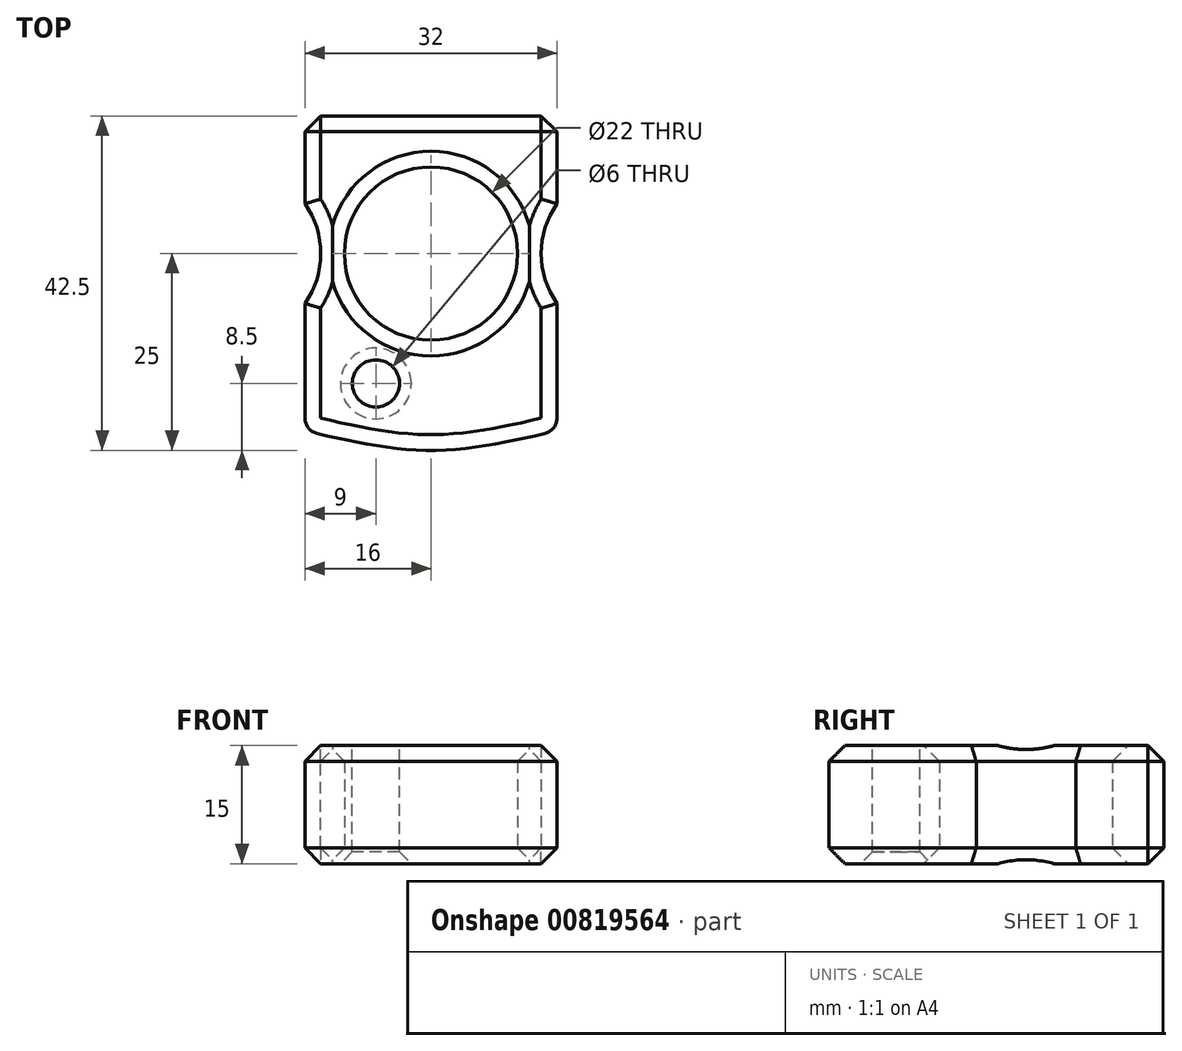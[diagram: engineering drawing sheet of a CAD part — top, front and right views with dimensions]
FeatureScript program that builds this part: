
annotation { "Feature Type Name" : "Feature", "Feature Type Description" : "" }
export const myFeature = defineFeature(function(context is Context, id is Id, definition is map)
    precondition{}
    {
        {
            var Q0;
            Q0=qCreatedBy(makeId("Top.planeOp"),FACE);
            var sketch = newSketch(context, id + "F0", { "sketchPlane" : qUnion([Q0])});
            skCircle(sketch, "E0", {"center": v(0, 0) * mm, "radius": 11 * mm});
            skLineSegment(sketch, "E1.left", {"start": v(16, -22.5) * mm, "end": v(16, -6.32) * mm});
            skLineSegment(sketch, "E1.right", {"start": v(-16, -22.5) * mm, "end": v(-16, -6.32) * mm});
            skArc(sketch, "E2", {"start": v(16, 6.32) * mm, "mid": v(14, 0) * mm, "end": v(16, -6.32) * mm});
            skArc(sketch, "E3", {"start": v(-16, -6.32) * mm, "mid": v(-14, 0) * mm, "end": v(-16, 6.32) * mm});
            skLineSegment(sketch, "E4.trimOffspring", {"start": v(-16, 6.32) * mm, "end": v(-16, 17.5) * mm});
            skLineSegment(sketch, "E5.trimOffspring", {"start": v(16, 6.32) * mm, "end": v(16, 17.5) * mm});
            skLineSegment(sketch, "E6", {"start": v(-11.23, -25) * mm, "end": v(12.92, -25) * mm, "construction": true});
            skLineSegment(sketch, "E7", {"start": v(-16, 17.5) * mm, "end": v(16, 17.5) * mm});
            skPoint(sketch, "E1.top.end.orphan", {"position": v(-16, 22.5) * mm});
            skPoint(sketch, "E1.top.start.orphan", {"position": v(16, 22.5) * mm});
            skFitSpline(sketch, "E8", {"points": [v(16, -22.5) * mm, v(0, -25) * mm, v(-16, -22.5) * mm], "startDerivative": vector(-32, -7.5) * mm, "endDerivative": vector(-32, 7.5) * mm});
            skSolve(sketch);
        }
        {
            var Q0;
            Q0 = qSketchRegion(id + "F0", true);
            extrude(context, id + "F1", {"entities" : qUnion([Q0]), "depth" : 15 * mm, "offsetDistance" : 25 * mm});
        }
        {
            var Q0;
            Q0=makeQuery(id+"F1.opExtrude","SWEPT_EDGE",EDGE,{"disambiguationData":[OSD([sQuery(id+"F0.wireOp",EDGE,"E1.right"),sQuery(id+"F0.wireOp",EDGE,"E8")])]});
            var Q1;
            Q1=makeQuery(id+"F1.opExtrude","SWEPT_EDGE",EDGE,{"disambiguationData":[OSD([sQuery(id+"F0.wireOp",EDGE,"E1.left"),sQuery(id+"F0.wireOp",EDGE,"E8")])]});
            fillet(context, id + "F2", {"entities" : qUnion([Q0, Q1]), "radius" : 2 * mm, "tangentPropagation" : true, "allowEdgeOverflow" : false});
        }
        {
            var Q0;
            Q0=makeQuery(id+"F1.opExtrude","CAP_FACE",FACE,{"disambiguationData":[OSD([sQuery(id+"F0.wireOp",EDGE,"E0"),sQuery(id+"F0.wireOp",EDGE,"E1.left"),sQuery(id+"F0.wireOp",EDGE,"E1.right"),sQuery(id+"F0.wireOp",EDGE,"E2"),sQuery(id+"F0.wireOp",EDGE,"E3"),sQuery(id+"F0.wireOp",EDGE,"E4.trimOffspring"),sQuery(id+"F0.wireOp",EDGE,"E5.trimOffspring"),sQuery(id+"F0.wireOp",EDGE,"E7"),sQuery(id+"F0.wireOp",EDGE,"E8")])],"isStart":false});
            var Q1;
            Q1=makeQuery(id+"F1.opExtrude","CAP_FACE",FACE,{"disambiguationData":[OSD([sQuery(id+"F0.wireOp",EDGE,"E0"),sQuery(id+"F0.wireOp",EDGE,"E1.left"),sQuery(id+"F0.wireOp",EDGE,"E1.right"),sQuery(id+"F0.wireOp",EDGE,"E2"),sQuery(id+"F0.wireOp",EDGE,"E3"),sQuery(id+"F0.wireOp",EDGE,"E4.trimOffspring"),sQuery(id+"F0.wireOp",EDGE,"E5.trimOffspring"),sQuery(id+"F0.wireOp",EDGE,"E7"),sQuery(id+"F0.wireOp",EDGE,"E8")])],"isStart":true});
            var Q2;
            Q2=makeQuery(id+"F1.opExtrude","SWEPT_EDGE",EDGE,{"disambiguationData":[OSD([sQuery(id+"F0.wireOp",EDGE,"E5.trimOffspring"),sQuery(id+"F0.wireOp",EDGE,"E7")])]});
            var Q3;
            Q3=makeQuery(id+"F1.opExtrude","SWEPT_EDGE",EDGE,{"disambiguationData":[OSD([sQuery(id+"F0.wireOp",EDGE,"E4.trimOffspring"),sQuery(id+"F0.wireOp",EDGE,"E7")])]});
            chamfer(context, id + "F3", {"entities" : qUnion([Q0, Q1, Q2, Q3]), "width" : 2 * mm, "tangentPropagation" : true});
        }
        {
            var Q0;
            Q0=makeQuery(id+"F3.opChamfer","SPLIT",FACE,{"disambiguationData":[OD(1.0)],"derivedFrom":makeQuery(id+"F1.opExtrude","CAP_FACE",FACE,{"disambiguationData":[OSD([sQuery(id+"F0.wireOp",EDGE,"E0"),sQuery(id+"F0.wireOp",EDGE,"E1.left"),sQuery(id+"F0.wireOp",EDGE,"E1.right"),sQuery(id+"F0.wireOp",EDGE,"E2"),sQuery(id+"F0.wireOp",EDGE,"E3"),sQuery(id+"F0.wireOp",EDGE,"E4.trimOffspring"),sQuery(id+"F0.wireOp",EDGE,"E5.trimOffspring"),sQuery(id+"F0.wireOp",EDGE,"E7"),sQuery(id+"F0.wireOp",EDGE,"E8")])],"isStart":false})});
            var sketch = newSketch(context, id + "F4", { "sketchPlane" : qUnion([Q0])});
            skLineSegment(sketch, "E9", {"start": v(-26.28, -16.5) * mm, "end": v(31.37, -16.5) * mm, "construction": true});
            skCircle(sketch, "E10", {"center": v(-7, -16.5) * mm, "radius": 3 * mm});
            skSolve(sketch);
        }
        {
            var Q0;
            Q0=makeQuery(id+"F4.imprint","IMPRINT",FACE,{"disambiguationData":[TD([[makeQuery(id+"F4.imprint","IMPRINT",EDGE,{"derivedFrom":sQuery(id+"F4.wireOp",EDGE,"E10")}),1.0]])]});
            var Q1;
            Q1=makeQuery(id+"F4.imprint","IMPRINT",FACE,{"disambiguationData":[TD([[makeQuery(id+"F4.imprint","IMPRINT",EDGE,{"derivedFrom":sQuery(id+"F4.wireOp",EDGE,"cAbSi6va-YZbb-ZV3Q-1W0d-QaFIP4ghxUrZ")}),1.0]])]});
            extrude(context, id + "F5", {"entities" : qUnion([Q0, Q1]), "operationType" : NewBodyOperationType.REMOVE, "oppositeDirection" : true, "depth" : 25 * mm, "offsetDistance" : 25 * mm});
        }
        {
            var Q0;
            Q0=makeQuery(id+"F5.boolean.opBoolean","COPY",EDGE,{"derivedFrom":makeQuery(id+"F5.opExtrude","CAP_EDGE",EDGE,{"disambiguationData":[OSD([sQuery(id+"F4.wireOp",EDGE,"E10")])],"isStart":true})});
            var Q1;
            Q1=makeQuery(id+"F5.boolean.opBoolean","COPY",EDGE,{"derivedFrom":makeQuery(id+"F5.opExtrude","CAP_EDGE",EDGE,{"disambiguationData":[OSD([sQuery(id+"F4.wireOp",EDGE,"cAbSi6va-YZbb-ZV3Q-1W0d-QaFIP4ghxUrZ")])],"isStart":true})});
            var Q2;
            Q2=makeQuery(id+"F5.boolean.opBoolean","INTERSECT",EDGE,{"derivedFrom":[makeQuery(id+"F3.opChamfer","SPLIT",FACE,{"disambiguationData":[OD(1.0)],"derivedFrom":makeQuery(id+"F1.opExtrude","CAP_FACE",FACE,{"disambiguationData":[OSD([sQuery(id+"F0.wireOp",EDGE,"E0"),sQuery(id+"F0.wireOp",EDGE,"E1.left"),sQuery(id+"F0.wireOp",EDGE,"E1.right"),sQuery(id+"F0.wireOp",EDGE,"E2"),sQuery(id+"F0.wireOp",EDGE,"E3"),sQuery(id+"F0.wireOp",EDGE,"E4.trimOffspring"),sQuery(id+"F0.wireOp",EDGE,"E5.trimOffspring"),sQuery(id+"F0.wireOp",EDGE,"E7"),sQuery(id+"F0.wireOp",EDGE,"E8")])],"isStart":true})}),makeQuery(id+"F5.opExtrude","SWEPT_FACE",FACE,{"disambiguationData":[OSD([sQuery(id+"F4.wireOp",EDGE,"E10")])]})]});
            var Q3;
            Q3=makeQuery(id+"F5.boolean.opBoolean","INTERSECT",EDGE,{"derivedFrom":[makeQuery(id+"F3.opChamfer","SPLIT",FACE,{"disambiguationData":[OD(1.0)],"derivedFrom":makeQuery(id+"F1.opExtrude","CAP_FACE",FACE,{"disambiguationData":[OSD([sQuery(id+"F0.wireOp",EDGE,"E0"),sQuery(id+"F0.wireOp",EDGE,"E1.left"),sQuery(id+"F0.wireOp",EDGE,"E1.right"),sQuery(id+"F0.wireOp",EDGE,"E2"),sQuery(id+"F0.wireOp",EDGE,"E3"),sQuery(id+"F0.wireOp",EDGE,"E4.trimOffspring"),sQuery(id+"F0.wireOp",EDGE,"E5.trimOffspring"),sQuery(id+"F0.wireOp",EDGE,"E7"),sQuery(id+"F0.wireOp",EDGE,"E8")])],"isStart":true})}),makeQuery(id+"F5.opExtrude","SWEPT_FACE",FACE,{"disambiguationData":[OSD([sQuery(id+"F4.wireOp",EDGE,"cAbSi6va-YZbb-ZV3Q-1W0d-QaFIP4ghxUrZ")])]})]});
            chamfer(context, id + "F6", {"entities" : qUnion([Q0, Q1, Q2, Q3]), "width" : 1.5 * mm, "tangentPropagation" : true});
        }
    });
